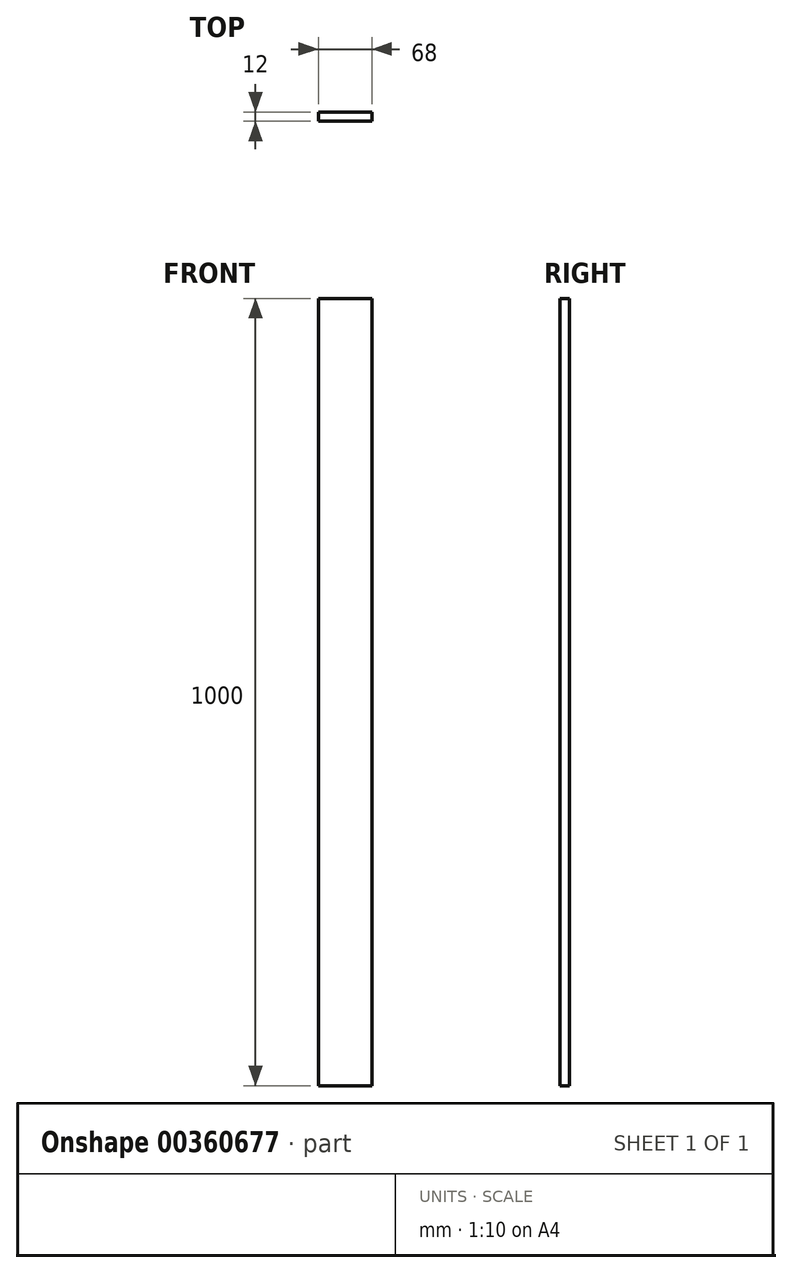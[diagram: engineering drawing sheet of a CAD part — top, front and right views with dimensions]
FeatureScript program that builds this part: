
annotation { "Feature Type Name" : "Feature", "Feature Type Description" : "" }
export const myFeature = defineFeature(function(context is Context, id is Id, definition is map)
    precondition{}
    {
        {
            var Q0;
            Q0=qCreatedBy(makeId("Front.planeOp"),FACE);
            var sketch = newSketch(context, id + "F0", { "sketchPlane" : qUnion([Q0])});
            skLineSegment(sketch, "E0.bottom", {"start": v(0, 0) * mm, "end": v(68, 0) * mm});
            skLineSegment(sketch, "E0.top", {"start": v(0, 1000) * mm, "end": v(68, 1000) * mm});
            skLineSegment(sketch, "E0.left", {"start": v(0, 0) * mm, "end": v(0, 1000) * mm});
            skLineSegment(sketch, "E0.right", {"start": v(68, 0) * mm, "end": v(68, 1000) * mm});
            skSolve(sketch);
        }
        {
            var Q0;
            Q0=makeQuery(id+"F0.imprint","IMPRINT",FACE,{"disambiguationData":[TD([[makeQuery(id+"F0.imprint","IMPRINT",EDGE,{"derivedFrom":sQuery(id+"F0.wireOp",EDGE,"E0.bottom")}),1.0]])]});
            extrude(context, id + "F1", {"entities" : qUnion([Q0]), "depth" : 12 * mm});
        }
    });
